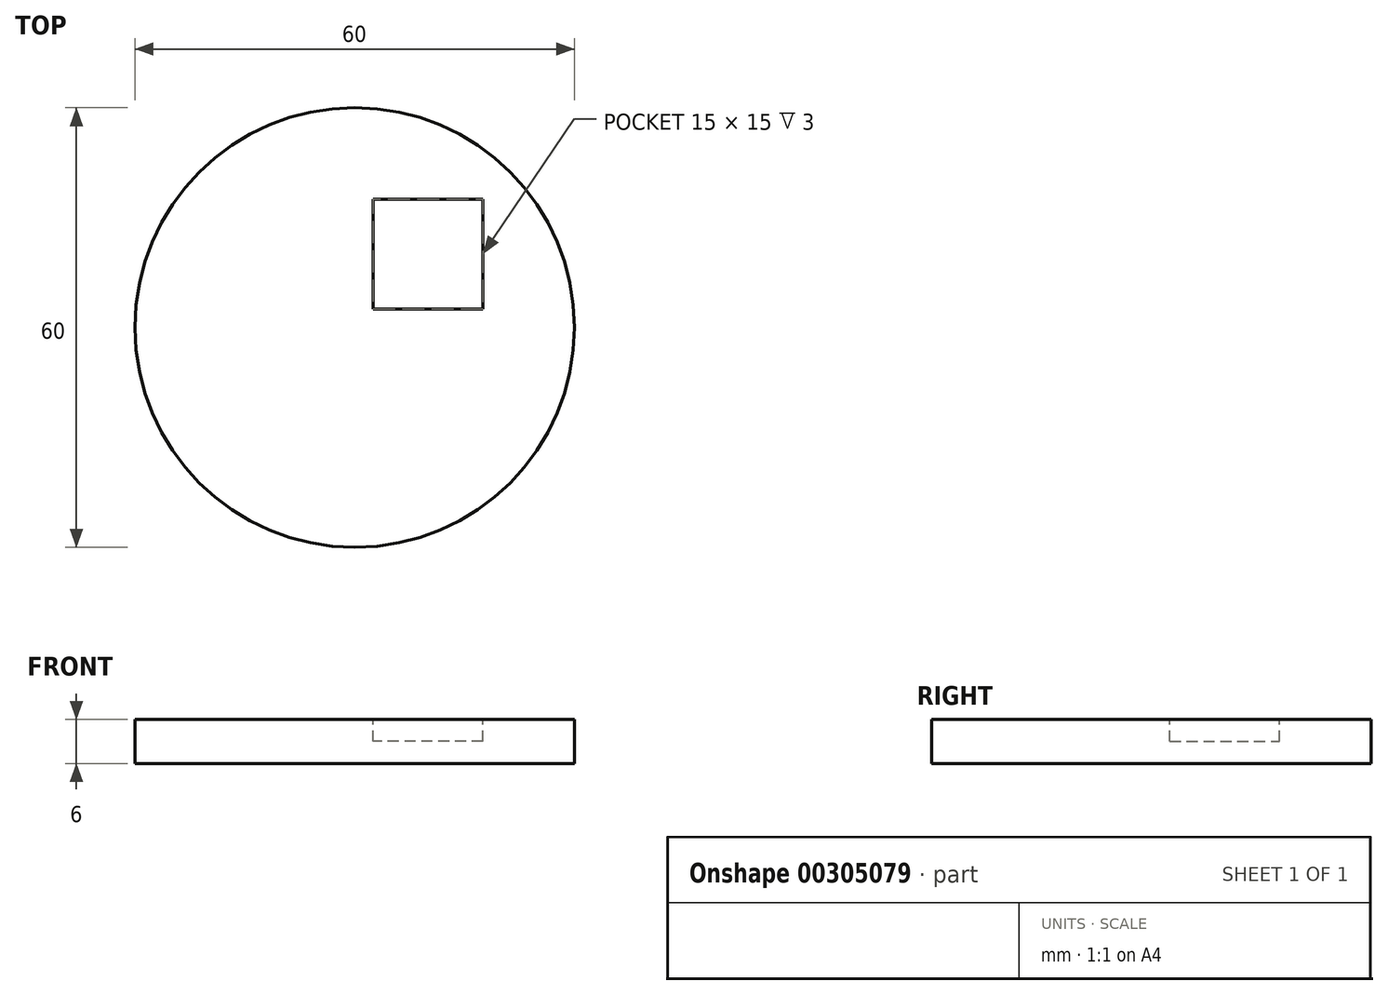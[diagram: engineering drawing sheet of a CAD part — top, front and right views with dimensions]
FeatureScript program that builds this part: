
annotation { "Feature Type Name" : "Feature", "Feature Type Description" : "" }
export const myFeature = defineFeature(function(context is Context, id is Id, definition is map)
    precondition{}
    {
        {
            var Q0;
            Q0=qCreatedBy(makeId("Top.planeOp"),FACE);
            var sketch = newSketch(context, id + "F0", { "sketchPlane" : qUnion([Q0])});
            skCircle(sketch, "E0", {"center": v(0, 0) * mm, "radius": 30 * mm});
            skSolve(sketch);
        }
        {
            var Q0;
            Q0 = qSketchRegion(id + "F0", true);
            extrude(context, id + "F1", {"entities" : qUnion([Q0]), "depth" : 6 * mm});
        }
        {
            var Q0;
            Q0=makeQuery(id+"F1.opExtrude","CAP_FACE",FACE,{"disambiguationData":[OSD([sQuery(id+"F0.wireOp",EDGE,"E0")])],"isStart":false});
            var sketch = newSketch(context, id + "F2", { "sketchPlane" : qUnion([Q0])});
            skLineSegment(sketch, "E1.bottom", {"start": v(17.5, 2.5) * mm, "end": v(2.5, 2.5) * mm});
            skLineSegment(sketch, "E1.top", {"start": v(17.5, 17.5) * mm, "end": v(2.5, 17.5) * mm});
            skLineSegment(sketch, "E1.left", {"start": v(17.5, 2.5) * mm, "end": v(17.5, 17.5) * mm});
            skLineSegment(sketch, "E1.right", {"start": v(2.5, 2.5) * mm, "end": v(2.5, 17.5) * mm});
            skPoint(sketch, "E1.middle", {"position": v(10, 10) * mm});
            skSolve(sketch);
        }
        {
            var Q0;
            Q0 = qSketchRegion(id + "F2", true);
            extrude(context, id + "F3", {"entities" : qUnion([Q0]), "operationType" : NewBodyOperationType.REMOVE, "oppositeDirection" : true, "depth" : 3 * mm});
        }
    });
